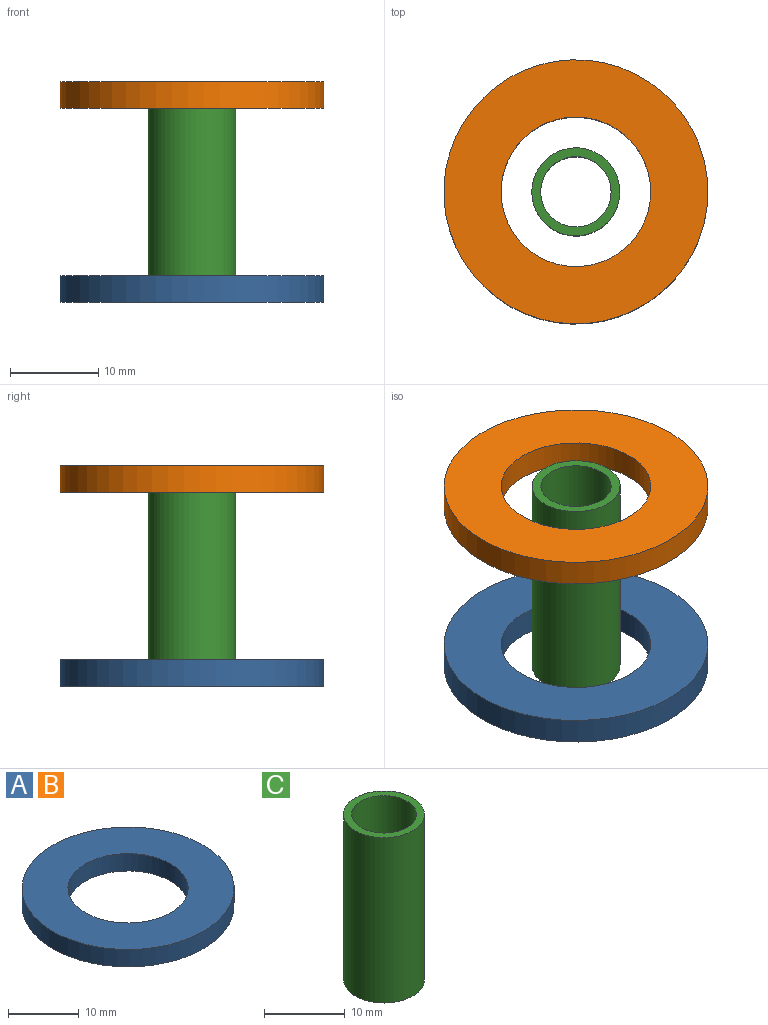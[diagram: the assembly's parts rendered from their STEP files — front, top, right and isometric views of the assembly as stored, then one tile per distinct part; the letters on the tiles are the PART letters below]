
ASSEMBLY  parts=3 mates=2
PART A: 4 faces, bbox 30x30x3 mm
  f0: cylinder r=8.5mm len=17mm, axis (0,0,-1), area 160.2mm2, adj f2,f3
  f1: cylinder r=15mm len=30mm, axis (0,0,-1), area 282.7mm2, adj f2,f3
  f2: plane 30x30mm, normal (0,0,1), area 479.9mm2, adj f0,f1
  f3: plane 30x30mm, normal (0,0,-1), area 479.9mm2, adj f0,f1
PART B: same geometry as A
PART C: 4 faces, bbox 10x10x25 mm
  f0: cylinder r=4mm len=25mm, axis (0,0,-1), area 628.3mm2, adj f2,f3
  f1: cylinder r=5mm len=25mm, axis (0,0,-1), area 785.4mm2, adj f2,f3
  f2: plane 10x10mm, normal (0,0,1), area 28.3mm2, adj f0,f1
  f3: plane 10x10mm, normal (0,0,-1), area 28.3mm2, adj f0,f1
PLACE A t=(-37.52,46.42,19.21)mm
PLACE B t=(-37.52,46.42,41.21)mm
PLACE C t=(12.27,13.72,19.21)mm
MATE fastened B.f0 <-> C.f0  axis (0,0,-1) through (-37.52,46.42,44.21)mm
MATE fastened A.f1 <-> C.f0  axis (0,0,-1) through (-37.52,46.42,19.21)mm
